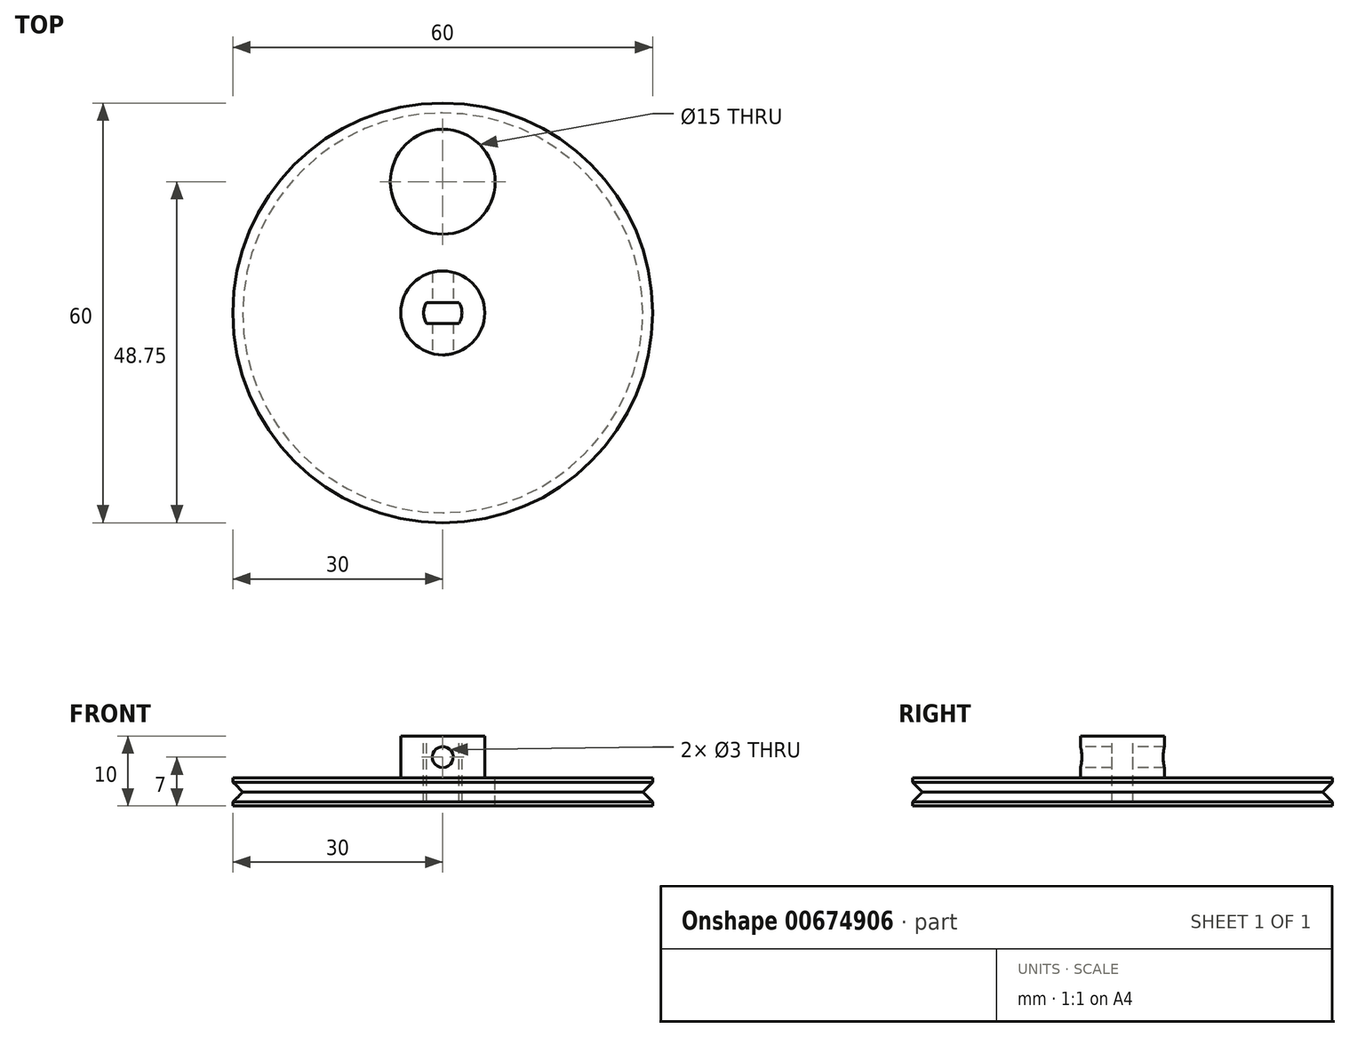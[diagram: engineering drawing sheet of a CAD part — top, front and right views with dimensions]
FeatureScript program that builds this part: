
annotation { "Feature Type Name" : "Feature", "Feature Type Description" : "" }
export const myFeature = defineFeature(function(context is Context, id is Id, definition is map)
    precondition{}
    {
        {
            var Q0;
            Q0=qCreatedBy(makeId("Top.planeOp"),FACE);
            var sketch = newSketch(context, id + "F0", { "sketchPlane" : qUnion([Q0])});
            skCircle(sketch, "E0", {"center": v(0, 0) * mm, "radius": 30 * mm});
            skCircle(sketch, "E1", {"center": v(0, 0) * mm, "radius": 6 * mm});
            skSolve(sketch);
        }
        {
            var Q0;
            Q0=makeQuery(id+"F0.imprint","IMPRINT",FACE,{"disambiguationData":[TD([[makeQuery(id+"F0.imprint","IMPRINT",EDGE,{"derivedFrom":sQuery(id+"F0.wireOp",EDGE,"E1")}),1.0]])]});
            var Q1;
            Q1=makeQuery(id+"F0.imprint","IMPRINT",FACE,{"disambiguationData":[TD([[makeQuery(id+"F0.imprint","IMPRINT",EDGE,{"derivedFrom":sQuery(id+"F0.wireOp",EDGE,"E0")}),1.0]])]});
            extrude(context, id + "F1", {"entities" : qUnion([Q0, Q1]), "oppositeDirection" : true, "depth" : 4 * mm, "offsetDistance" : 25 * mm});
        }
        {
            var Q0;
            Q0=makeQuery(id+"F0.imprint","IMPRINT",FACE,{"disambiguationData":[TD([[makeQuery(id+"F0.imprint","IMPRINT",EDGE,{"derivedFrom":sQuery(id+"F0.wireOp",EDGE,"E1")}),1.0]])]});
            extrude(context, id + "F2", {"entities" : qUnion([Q0]), "operationType" : NewBodyOperationType.ADD, "depth" : 6 * mm, "offsetDistance" : 25 * mm});
        }
        {
            var Q0;
            Q0=qCreatedBy(makeId("Front.planeOp"),FACE);
            var sketch = newSketch(context, id + "F3", { "sketchPlane" : qUnion([Q0])});
            skCircle(sketch, "E2", {"center": v(0, 3) * mm, "radius": 1.5 * mm});
            skSolve(sketch);
        }
        {
            var Q0;
            Q0=qSketchRegion(id+"F3",true);
            extrude(context, id + "F4", {"entities" : qUnion([Q0]), "operationType" : NewBodyOperationType.REMOVE, "endBound" : BoundingType.SYMMETRIC, "oppositeDirection" : true, "depth" : 25 * mm, "offsetDistance" : 25 * mm});
        }
        {
            var Q0;
            Q0=makeQuery(id+"F2.opExtrude","CAP_FACE",FACE,{"disambiguationData":[OSD([sQuery(id+"F0.wireOp",EDGE,"E1")])],"isStart":false});
            var sketch = newSketch(context, id + "F5", { "sketchPlane" : qUnion([Q0])});
            skLineSegment(sketch, "E3.bottom", {"start": v(-2.3, -1.5) * mm, "end": v(2.3, -1.5) * mm});
            skLineSegment(sketch, "E3.top", {"start": v(-2.3, 1.5) * mm, "end": v(2.3, 1.5) * mm});
            skLineSegment(sketch, "E3.left", {"start": v(-2.3, -1.5) * mm, "end": v(-2.3, 1.5) * mm});
            skLineSegment(sketch, "E3.right", {"start": v(2.3, -1.5) * mm, "end": v(2.3, 1.5) * mm});
            skPoint(sketch, "E3.middle", {"position": v(0, 0) * mm});
            skArc(sketch, "E4", {"start": v(-2.3, 1.5) * mm, "mid": v(-2.75, 0) * mm, "end": v(-2.3, -1.5) * mm});
            skArc(sketch, "E5", {"start": v(2.3, -1.5) * mm, "mid": v(2.75, 0) * mm, "end": v(2.3, 1.5) * mm});
            skSolve(sketch);
        }
        {
            var Q0;
            Q0=qSketchRegion(id+"F5",true);
            extrude(context, id + "F6", {"entities" : qUnion([Q0]), "operationType" : NewBodyOperationType.REMOVE, "oppositeDirection" : true, "depth" : 9.4 * mm, "offsetDistance" : 25 * mm});
        }
        {
            var Q0;
            Q0=qCreatedBy(makeId("Front.planeOp"),FACE);
            var sketch = newSketch(context, id + "F7", { "sketchPlane" : qUnion([Q0])});
            skLineSegment(sketch, "E6", {"start": v(30, 0) * mm, "end": v(30, -4) * mm, "construction": true});
            skLineSegment(sketch, "E7", {"start": v(30, -0.59) * mm, "end": v(28.59, -2) * mm});
            skLineSegment(sketch, "E8", {"start": v(28.59, -2) * mm, "end": v(30, -3.41) * mm});
            skLineSegment(sketch, "E9", {"start": v(30, -2) * mm, "end": v(25.84, -2) * mm, "construction": true});
            skLineSegment(sketch, "E10", {"start": v(0, 13.1) * mm, "end": v(0, -11.57) * mm, "construction": true});
            skLineSegment(sketch, "E11", {"start": v(30, -0.59) * mm, "end": v(30, -3.41) * mm});
            skSolve(sketch);
        }
        {
            var Q0;
            Q0=qSketchRegion(id+"F7",true);
            var Q1;
            Q1=qConstructionFilter(qBodyType(qCreatedBy(id+"F7",EDGE),BodyType.WIRE),ConstructionObject.NO);
            var Q2;
            Q2=sQuery(id+"F7.wireOp",EDGE,"E10");
            revolve(context, id + "F8", {"operationType" : NewBodyOperationType.REMOVE, "entities" : qUnion([Q0]), "surfaceEntities" : qUnion([Q1]), "axis" : qUnion([Q2]), "revolveType" : RevolveType.FULL, "oppositeDirection" : true});
        }
        {
            var Q0;
            Q0=makeQuery(id+"F0.imprint","IMPRINT",FACE,{"disambiguationData":[TD([[makeQuery(id+"F0.imprint","IMPRINT",EDGE,{"derivedFrom":sQuery(id+"F0.wireOp",EDGE,"E0")}),1.0]])]});
            var sketch = newSketch(context, id + "F9", { "sketchPlane" : qUnion([Q0])});
            skCircle(sketch, "E12", {"center": v(0, 18.75) * mm, "radius": 7.5 * mm});
            skSolve(sketch);
        }
        {
            var Q0;
            Q0=qSketchRegion(id+"F9",true);
            extrude(context, id + "F10", {"entities" : qUnion([Q0]), "operationType" : NewBodyOperationType.REMOVE, "oppositeDirection" : true, "depth" : 25 * mm, "offsetDistance" : 25 * mm});
        }
    });
